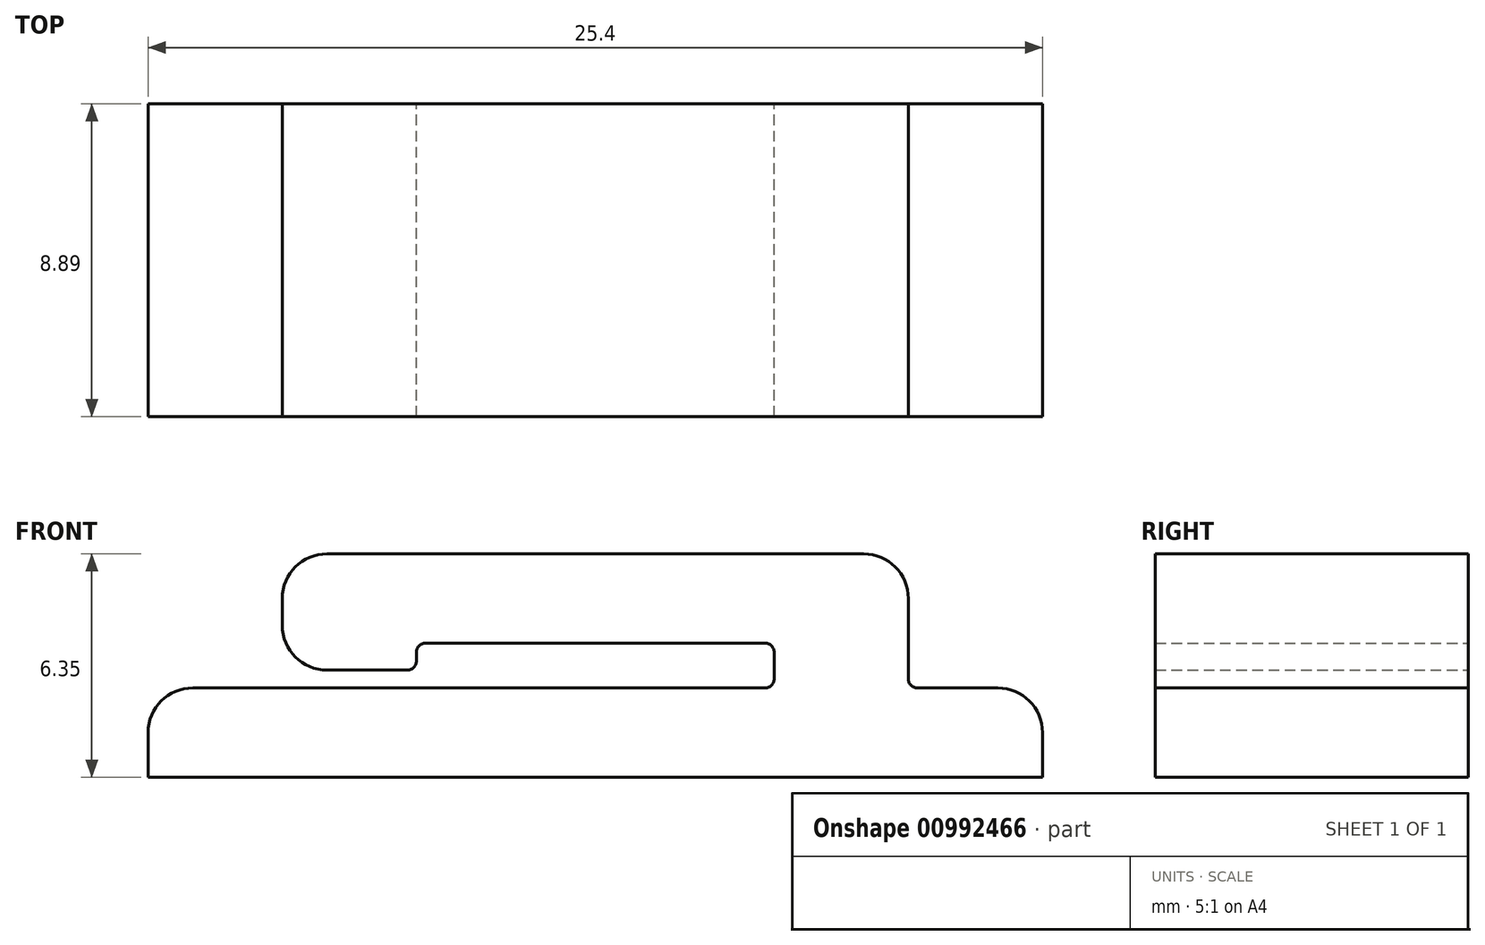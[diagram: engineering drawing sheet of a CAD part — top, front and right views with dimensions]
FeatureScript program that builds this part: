
annotation { "Feature Type Name" : "Feature", "Feature Type Description" : "" }
export const myFeature = defineFeature(function(context is Context, id is Id, definition is map)
    precondition{}
    {
        {
            var Q0;
            Q0=qCreatedBy(makeId("Front.planeOp"),FACE);
            var sketch = newSketch(context, id + "F0", { "sketchPlane" : qUnion([Q0])});
            skLineSegment(sketch, "E0", {"start": v(-102.72, 0) * mm, "end": v(-77.32, 0) * mm});
            skLineSegment(sketch, "E1", {"start": v(-77.32, 0) * mm, "end": v(-77.32, 1.27) * mm});
            skLineSegment(sketch, "E2", {"start": v(-78.6, 2.54) * mm, "end": v(-80.88, 2.54) * mm});
            skLineSegment(sketch, "E3", {"start": v(-81.13, 2.8) * mm, "end": v(-81.13, 5.08) * mm});
            skLineSegment(sketch, "E4", {"start": v(-82.4, 6.35) * mm, "end": v(-97.64, 6.35) * mm});
            skLineSegment(sketch, "E5", {"start": v(-98.91, 5.08) * mm, "end": v(-98.91, 4.32) * mm});
            skLineSegment(sketch, "E6", {"start": v(-97.64, 3.05) * mm, "end": v(-95.36, 3.05) * mm});
            skLineSegment(sketch, "E7", {"start": v(-95.1, 3.3) * mm, "end": v(-95.1, 3.56) * mm});
            skLineSegment(sketch, "E8", {"start": v(-94.85, 3.81) * mm, "end": v(-85.2, 3.81) * mm});
            skLineSegment(sketch, "E9", {"start": v(-84.94, 3.56) * mm, "end": v(-84.94, 2.8) * mm});
            skLineSegment(sketch, "E10", {"start": v(-85.2, 2.54) * mm, "end": v(-101.45, 2.54) * mm});
            skLineSegment(sketch, "E11", {"start": v(-102.72, 1.27) * mm, "end": v(-102.72, 0) * mm});
            skPoint(sketch, "E12.visualSharp", {"position": v(-102.72, 2.54) * mm});
            skArc(sketch, "E12.filletArc", {"start": v(-101.45, 2.54) * mm, "mid": v(-102.35, 2.17) * mm, "end": v(-102.72, 1.27) * mm});
            skPoint(sketch, "E13.visualSharp", {"position": v(-77.32, 2.54) * mm});
            skArc(sketch, "E13.filletArc", {"start": v(-77.32, 1.27) * mm, "mid": v(-77.7, 2.17) * mm, "end": v(-78.6, 2.54) * mm});
            skPoint(sketch, "E14.visualSharp", {"position": v(-98.91, 6.35) * mm});
            skArc(sketch, "E14.filletArc", {"start": v(-97.64, 6.35) * mm, "mid": v(-98.54, 5.98) * mm, "end": v(-98.91, 5.08) * mm});
            skPoint(sketch, "E15.visualSharp", {"position": v(-81.13, 6.35) * mm});
            skArc(sketch, "E15.filletArc", {"start": v(-81.13, 5.08) * mm, "mid": v(-81.5, 5.98) * mm, "end": v(-82.4, 6.35) * mm});
            skPoint(sketch, "E16.visualSharp", {"position": v(-98.91, 3.05) * mm});
            skArc(sketch, "E16.filletArc", {"start": v(-98.91, 4.32) * mm, "mid": v(-98.54, 3.42) * mm, "end": v(-97.64, 3.05) * mm});
            skPoint(sketch, "E17.visualSharp", {"position": v(-95.1, 3.05) * mm});
            skArc(sketch, "E17.filletArc", {"start": v(-95.36, 3.05) * mm, "mid": v(-95.18, 3.12) * mm, "end": v(-95.1, 3.3) * mm});
            skPoint(sketch, "E18.visualSharp", {"position": v(-95.1, 3.81) * mm});
            skArc(sketch, "E18.filletArc", {"start": v(-94.85, 3.81) * mm, "mid": v(-95.03, 3.74) * mm, "end": v(-95.1, 3.56) * mm});
            skPoint(sketch, "E19.visualSharp", {"position": v(-84.94, 3.81) * mm});
            skArc(sketch, "E19.filletArc", {"start": v(-84.94, 3.56) * mm, "mid": v(-85.02, 3.74) * mm, "end": v(-85.2, 3.81) * mm});
            skPoint(sketch, "E20.visualSharp", {"position": v(-84.94, 2.54) * mm});
            skArc(sketch, "E20.filletArc", {"start": v(-85.2, 2.54) * mm, "mid": v(-85.02, 2.61) * mm, "end": v(-84.94, 2.8) * mm});
            skPoint(sketch, "E21.visualSharp", {"position": v(-81.13, 2.54) * mm});
            skArc(sketch, "E21.filletArc", {"start": v(-81.13, 2.8) * mm, "mid": v(-81.06, 2.61) * mm, "end": v(-80.88, 2.54) * mm});
            skSolve(sketch);
        }
        {
            var Q0;
            Q0=makeQuery(id+"F0.imprint","IMPRINT",FACE,{"disambiguationData":[TD([[makeQuery(id+"F0.imprint","IMPRINT",EDGE,{"derivedFrom":sQuery(id+"F0.wireOp",EDGE,"E0")}),1.0]])]});
            extrude(context, id + "F1", {"entities" : qUnion([Q0]), "depth" : 8.9 * mm, "offsetDistance" : 25.4 * mm});
        }
    });
